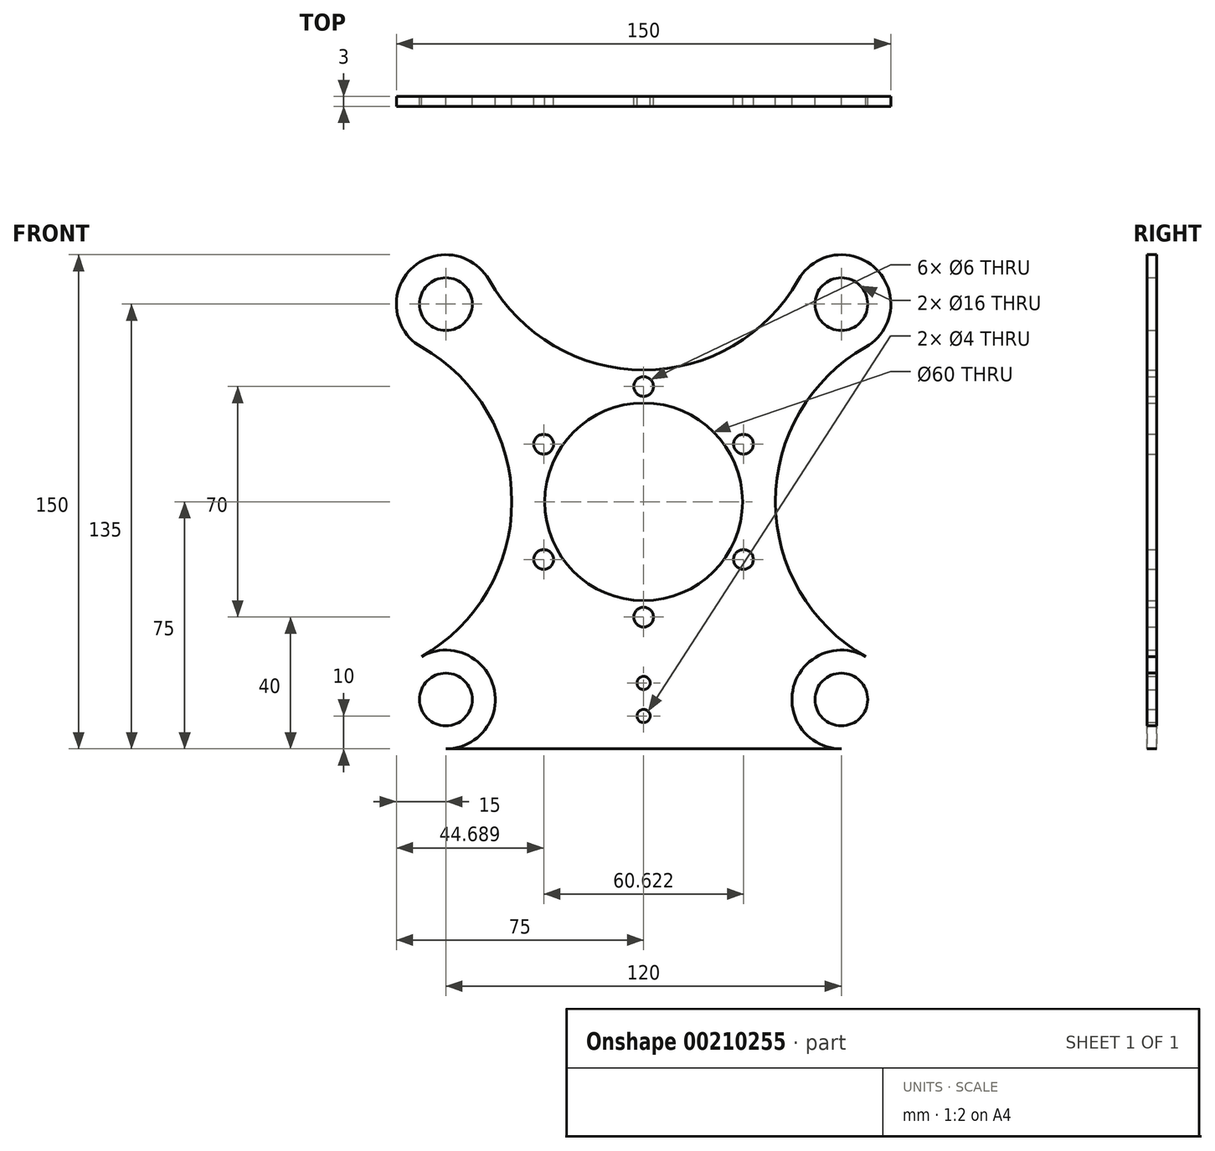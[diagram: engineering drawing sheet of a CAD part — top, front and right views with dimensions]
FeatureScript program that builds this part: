
annotation { "Feature Type Name" : "Feature", "Feature Type Description" : "" }
export const myFeature = defineFeature(function(context is Context, id is Id, definition is map)
    precondition{}
    {
        {
            var Q0;
            Q0=qCreatedBy(makeId("Front.planeOp"),FACE);
            var sketch = newSketch(context, id + "F0", { "sketchPlane" : qUnion([Q0])});
            skCircle(sketch, "E0", {"center": v(0, 0) * mm, "radius": 40 * mm});
            skCircle(sketch, "E1", {"center": v(-60, 60) * mm, "radius": 15 * mm});
            skCircle(sketch, "E2", {"center": v(60, 60) * mm, "radius": 15 * mm});
            skCircle(sketch, "E3", {"center": v(-60, 60) * mm, "radius": 8 * mm});
            skCircle(sketch, "E4", {"center": v(60, 60) * mm, "radius": 8 * mm});
            skArc(sketch, "E5", {"start": v(-46.94, 67.38) * mm, "mid": v(-27.17, 47.35) * mm, "end": v(0, 40) * mm});
            skArc(sketch, "E6", {"start": v(0, 40) * mm, "mid": v(27.17, 47.35) * mm, "end": v(46.94, 67.38) * mm});
            skCircle(sketch, "E7", {"center": v(0, 0) * mm, "radius": 30 * mm});
            skCircle(sketch, "E8.MirrorC", {"center": v(-60, -60) * mm, "radius": 15 * mm});
            skCircle(sketch, "E9.MirrorC", {"center": v(-60, -60) * mm, "radius": 8 * mm});
            skCircle(sketch, "E10.MirrorC", {"center": v(60, -60) * mm, "radius": 8 * mm});
            skCircle(sketch, "E11.MirrorC", {"center": v(60, -60) * mm, "radius": 15 * mm});
            skArc(sketch, "E12", {"start": v(-40, 0) * mm, "mid": v(-47.35, 27.17) * mm, "end": v(-67.38, 46.94) * mm});
            skArc(sketch, "E13", {"start": v(-67.38, -46.94) * mm, "mid": v(-47.35, -27.17) * mm, "end": v(-40, 0) * mm});
            skArc(sketch, "E14", {"start": v(67.38, 46.94) * mm, "mid": v(47.35, 27.17) * mm, "end": v(40, 0) * mm});
            skArc(sketch, "E15", {"start": v(40, 0) * mm, "mid": v(47.35, -27.17) * mm, "end": v(67.38, -46.94) * mm});
            skLineSegment(sketch, "E16", {"start": v(-60, -75) * mm, "end": v(60, -75) * mm});
            skCircle(sketch, "E17", {"center": v(0, -65) * mm, "radius": 2 * mm});
            skCircle(sketch, "E18", {"center": v(0, -55) * mm, "radius": 2 * mm});
            skCircle(sketch, "E19", {"center": v(0, 35) * mm, "radius": 3 * mm});
            skCircle(sketch, "E20.1.0", {"center": v(-30.31, 17.5) * mm, "radius": 3 * mm});
            skCircle(sketch, "E20.2.0", {"center": v(-30.31, -17.5) * mm, "radius": 3 * mm});
            skCircle(sketch, "E20.3.0", {"center": v(0, -35) * mm, "radius": 3 * mm});
            skCircle(sketch, "E20.4.0", {"center": v(30.31, -17.5) * mm, "radius": 3 * mm});
            skCircle(sketch, "E20.5.0", {"center": v(30.31, 17.5) * mm, "radius": 3 * mm});
            skSolve(sketch);
        }
        {
            var Q0;
            Q0=makeQuery(id+"F0.imprint","IMPRINT",FACE,{"disambiguationData":[TD([[makeQuery(id+"F0.imprint","IMPRINT",EDGE,{"derivedFrom":sQuery(id+"F0.wireOp",EDGE,"E3")}),-1.0]])]});
            var Q1;
            {var subQ0=sQuery(id+"F0.wireOp",EDGE,"E5");Q1=makeQuery(id+"F0.imprint","IMPRINT",FACE,{"disambiguationData":[TD([[makeQuery(id+"F0.imprint","IMPRINT",EDGE,{"derivedFrom":subQ0}),-1.0]])]});}
            var Q2;
            Q2=makeQuery(id+"F0.imprint","IMPRINT",FACE,{"disambiguationData":[TD([[makeQuery(id+"F0.imprint","IMPRINT",EDGE,{"derivedFrom":sQuery(id+"F0.wireOp",EDGE,"E7")}),-1.0]])]});
            var Q3;
            {var subQ0=sQuery(id+"F0.wireOp",EDGE,"E6");Q3=makeQuery(id+"F0.imprint","IMPRINT",FACE,{"disambiguationData":[TD([[makeQuery(id+"F0.imprint","IMPRINT",EDGE,{"derivedFrom":subQ0}),-1.0]])]});}
            var Q4;
            Q4=makeQuery(id+"F0.imprint","IMPRINT",FACE,{"disambiguationData":[TD([[makeQuery(id+"F0.imprint","IMPRINT",EDGE,{"derivedFrom":sQuery(id+"F0.wireOp",EDGE,"E4")}),-1.0]])]});
            var Q5;
            {var subQ0=sQuery(id+"F0.wireOp",EDGE,"E13");Q5=makeQuery(id+"F0.imprint","IMPRINT",FACE,{"disambiguationData":[TD([[makeQuery(id+"F0.imprint","IMPRINT",EDGE,{"derivedFrom":subQ0}),-1.0]])]});}
            var Q6;
            Q6=makeQuery(id+"F0.imprint","IMPRINT",FACE,{"disambiguationData":[TD([[makeQuery(id+"F0.imprint","IMPRINT",EDGE,{"derivedFrom":sQuery(id+"F0.wireOp",EDGE,"E9.MirrorC")}),1.0]])]});
            var Q7;
            Q7=makeQuery(id+"F0.imprint","IMPRINT",FACE,{"disambiguationData":[TD([[makeQuery(id+"F0.imprint","IMPRINT",EDGE,{"derivedFrom":sQuery(id+"F0.wireOp",EDGE,"E10.MirrorC")}),1.0]])]});
            extrude(context, id + "F1", {"entities" : qUnion([Q0, Q1, Q2, Q3, Q4, Q5, Q6, Q7]), "depth" : 3 * mm});
        }
    });
